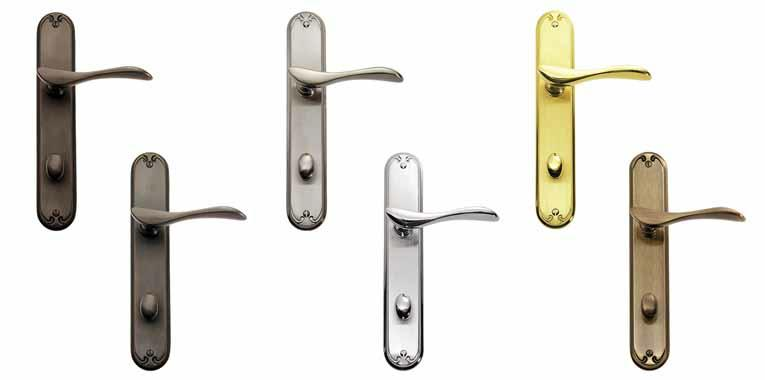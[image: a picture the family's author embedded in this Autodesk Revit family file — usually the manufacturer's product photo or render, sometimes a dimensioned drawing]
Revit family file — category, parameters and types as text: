
# Revit family: Door-French-Pella-Architect_Series-Hinged_Patio_Door-InSwing-Active_Passive
name_source: partatom
category: Doors
revit_build: Autodesk Revit Architecture 2013 (Build: 20130531_2115(x64)
units: mm (PartAtom-declared; Revit-internal decimal feet)

## types (30) — shared parameters
Analytic Construction = <None>
Architectural Design Manual = www.pellaadm.com
Construction Type = -
Cross Grille Pattern = No
Custom Grille Pattern = No
Custom Horizontal Lites = 2
Custom Vertical Lites = 6
Description = In-Swing French - Active / Passive Operation
Door Grille Visibility = Yes
Door Handle Height = 3' - 0"
Energy Efficiency = http://www.pella.com
Environmental Commitment = http://www.pella.com
Ext Finish = Aluminum - Pella - Brown
Function = Interior
Glazing Finish = Glass - Pella - Clear Insulating Glass
Glazing Thickness = 107/128"
Int Finish = Wood - Pella - Pine
Manufacturer = Pella - Windows & Doors
Note* = Maximum Frame Depth is 211 mm; if Wall Depth exceeds this value please recalculated Set Back to reflect
Operation = Hinged Patio Door
Prairie Grille Pattern = No
Product Documentation Link = http://media.pella.com
Product Name = Architect Series Hinged Patio Door
Product Page URL = http://www.pella.com
Series = Architect Series - Aluminum-Clad Wood
Top Row Grille Pattern = No
Traditional Grille Pattern = Yes
URL = www.pella.com
Wall Closure = By host

## per-type parameters (varying)
| type | C Height | C Width | DLO Height | DLO Width | Height | Hinges | Rough Height | Rough Width | Unit Height | Unit Width | Width |
| 5080 | 6' - 7 1/2" | 4' - 2" | 5' - 3 105/256" | 1' - 0 121/128" | 6' - 7 1/2" | 3 | 6' - 8" | 4' - 2 3/4" | 6' - 4 5/8" | 1' - 11 23/256" | 4' - 2" |
| 5081 | 6' - 8 1/8" | 4' - 2" | 5' - 4 9/256" | 1' - 0 121/128" | 6' - 8 1/8" | 3 | 6' - 8 5/8" | 4' - 2 3/4" | 6' - 5 1/4" | 1' - 11 23/256" | 4' - 2" |
| 5082 | 6' - 9 1/4" | 4' - 2" | 5' - 5 41/256" | 1' - 0 121/128" | 6' - 9 1/4" | 3 | 6' - 9 3/4" | 4' - 2 3/4" | 6' - 6 3/8" | 1' - 11 23/256" | 4' - 2" |
| 5086 | 7' - 2" | 4' - 2" | 5' - 9 233/256" | 1' - 0 121/128" | 7' - 2" | 4 | 7' - 2 1/2" | 4' - 2 3/4" | 6' - 11 1/8" | 1' - 11 23/256" | 4' - 2" |
| 5096 | 7' - 11 1/2" | 4' - 2" | 6' - 7 105/256" | 1' - 0 121/128" | 7' - 11 1/2" | 4 | 8' - 0" | 4' - 2 3/4" | 7' - 8 5/8" | 1' - 11 23/256" | 4' - 2" |
| 50120 | 9' - 11 1/4" | 4' - 2" | 8' - 7 41/256" | 1' - 0 121/128" | 9' - 11 1/4" | 4 | 9' - 11 3/4" | 4' - 2 3/4" | 9' - 8 3/8" | 1' - 11 23/256" | 4' - 2" |
| 6080 | 6' - 7 1/2" | 4' - 11 1/4" | 5' - 3 105/256" | 1' - 5 73/128" | 6' - 7 1/2" | 3 | 6' - 8" | 5' - 0" | 6' - 4 5/8" | 2' - 3 183/256" | 4' - 11 1/4" |
| 6081 | 6' - 8 1/8" | 4' - 11 1/4" | 5' - 4 9/256" | 1' - 5 73/128" | 6' - 8 1/8" | 3 | 6' - 8 5/8" | 5' - 0" | 6' - 5 1/4" | 2' - 3 183/256" | 4' - 11 1/4" |
| 6082 | 6' - 9 1/4" | 4' - 11 1/4" | 5' - 5 41/256" | 1' - 5 73/128" | 6' - 9 1/4" | 3 | 6' - 9 3/4" | 5' - 0" | 6' - 6 3/8" | 2' - 3 183/256" | 4' - 11 1/4" |
| 6086 | 7' - 2" | 4' - 11 1/4" | 5' - 9 233/256" | 1' - 5 73/128" | 7' - 2" | 4 | 7' - 2 1/2" | 5' - 0" | 6' - 11 1/8" | 2' - 3 183/256" | 4' - 11 1/4" |
| 6096 | 7' - 11 1/2" | 4' - 11 1/4" | 6' - 7 105/256" | 1' - 5 73/128" | 7' - 11 1/2" | 4 | 8' - 0" | 5' - 0" | 7' - 8 5/8" | 2' - 3 183/256" | 4' - 11 1/4" |
| 60120 | 9' - 11 1/4" | 4' - 11 1/4" | 8' - 7 41/256" | 1' - 5 73/128" | 9' - 11 1/4" | 4 | 9' - 11 3/4" | 5' - 0" | 9' - 8 3/8" | 2' - 3 183/256" | 4' - 11 1/4" |
| 6780 | 6' - 7 1/2" | 5' - 6 1/4" | 5' - 3 105/256" | 1' - 9 9/128" | 6' - 7 1/2" | 3 | 6' - 8" | 5' - 7" | 6' - 4 5/8" | 2' - 7 55/256" | 5' - 6 1/4" |
| 6781 | 6' - 8 1/8" | 5' - 6 1/4" | 5' - 4 9/256" | 1' - 9 9/128" | 6' - 8 1/8" | 3 | 6' - 8 5/8" | 5' - 7" | 6' - 5 1/4" | 2' - 7 55/256" | 5' - 6 1/4" |
| 6782 | 6' - 9 1/4" | 5' - 6 1/4" | 5' - 5 41/256" | 1' - 9 9/128" | 6' - 9 1/4" | 3 | 6' - 9 3/4" | 5' - 7" | 6' - 6 3/8" | 2' - 7 55/256" | 5' - 6 1/4" |
| 6786 | 7' - 2" | 5' - 6 1/4" | 5' - 9 233/256" | 1' - 9 9/128" | 7' - 2" | 4 | 7' - 2 1/2" | 5' - 7" | 6' - 11 1/8" | 2' - 7 55/256" | 5' - 6 1/4" |
| 6796 | 7' - 11 1/2" | 5' - 6 1/4" | 6' - 7 105/256" | 1' - 9 9/128" | 7' - 11 1/2" | 4 | 8' - 0" | 5' - 7" | 7' - 8 5/8" | 2' - 7 55/256" | 5' - 6 1/4" |
| 67120 | 9' - 11 1/4" | 5' - 6 1/4" | 8' - 7 41/256" | 1' - 9 9/128" | 9' - 11 1/4" | 4 | 9' - 11 3/4" | 5' - 7" | 9' - 8 3/8" | 2' - 7 55/256" | 5' - 6 1/4" |
| 7280 | 6' - 7 1/2" | 5' - 11 1/4" | 5' - 3 105/256" | 1' - 11 73/128" | 6' - 7 1/2" | 3 | 6' - 8" | 6' - 0" | 6' - 4 5/8" | 2' - 9 183/256" | 5' - 11 1/4" |
| 7281 | 6' - 8 1/8" | 5' - 11 1/4" | 5' - 4 9/256" | 1' - 11 73/128" | 6' - 8 1/8" | 3 | 6' - 8 5/8" | 6' - 0" | 6' - 5 1/4" | 2' - 9 183/256" | 5' - 11 1/4" |
| 7282 | 6' - 9 1/4" | 5' - 11 1/4" | 5' - 5 41/256" | 1' - 11 73/128" | 6' - 9 1/4" | 3 | 6' - 9 3/4" | 6' - 0" | 6' - 6 3/8" | 2' - 9 183/256" | 5' - 11 1/4" |
| 7286 | 7' - 2" | 5' - 11 1/4" | 5' - 9 233/256" | 1' - 11 73/128" | 7' - 2" | 4 | 7' - 2 1/2" | 6' - 0" | 6' - 11 1/8" | 2' - 9 183/256" | 5' - 11 1/4" |
| 7296 | 7' - 11 1/2" | 5' - 11 1/4" | 6' - 7 105/256" | 1' - 11 73/128" | 7' - 11 1/2" | 4 | 8' - 0" | 6' - 0" | 7' - 8 5/8" | 2' - 9 183/256" | 5' - 11 1/4" |
| 72120 | 9' - 11 1/4" | 5' - 11 1/4" | 8' - 7 41/256" | 1' - 11 73/128" | 9' - 11 1/4" | 4 | 9' - 11 3/4" | 6' - 0" | 9' - 8 3/8" | 2' - 9 183/256" | 5' - 11 1/4" |
| 7580 | 6' - 7 1/2" | 6' - 3" | 5' - 3 105/256" | 2' - 1 57/128" | 6' - 7 1/2" | 3 | 6' - 8" | 6' - 3 3/4" | 6' - 4 5/8" | 2' - 11 151/256" | 6' - 3" |
| 7581 | 6' - 8 1/8" | 6' - 3" | 5' - 4 9/256" | 2' - 1 57/128" | 6' - 8 1/8" | 3 | 6' - 8 5/8" | 6' - 3 3/4" | 6' - 5 1/4" | 2' - 11 151/256" | 6' - 3" |
| 7582 | 6' - 9 1/4" | 6' - 3" | 5' - 5 41/256" | 2' - 1 57/128" | 6' - 9 1/4" | 3 | 6' - 9 3/4" | 6' - 3 3/4" | 6' - 6 3/8" | 2' - 11 151/256" | 6' - 3" |
| 7586 | 7' - 2" | 6' - 3" | 5' - 9 233/256" | 2' - 1 57/128" | 7' - 2" | 4 | 7' - 2 1/2" | 6' - 3 3/4" | 6' - 11 1/8" | 2' - 11 151/256" | 6' - 3" |
| 7596 | 7' - 11 1/2" | 6' - 3" | 6' - 7 105/256" | 2' - 1 57/128" | 7' - 11 1/2" | 4 | 8' - 0" | 6' - 3 3/4" | 7' - 8 5/8" | 2' - 11 151/256" | 6' - 3" |
| 75120 | 9' - 11 1/4" | 6' - 3" | 8' - 7 41/256" | 2' - 1 57/128" | 9' - 11 1/4" | 4 | 9' - 11 3/4" | 6' - 3 3/4" | 9' - 8 3/8" | 2' - 11 151/256" | 6' - 3" |

note: column(s) folded — value = type name in every type: Model

## geometry (parser evidence)
native form markers: Blend x6, Sweep x9
no freeform markers — native parametric forms only
